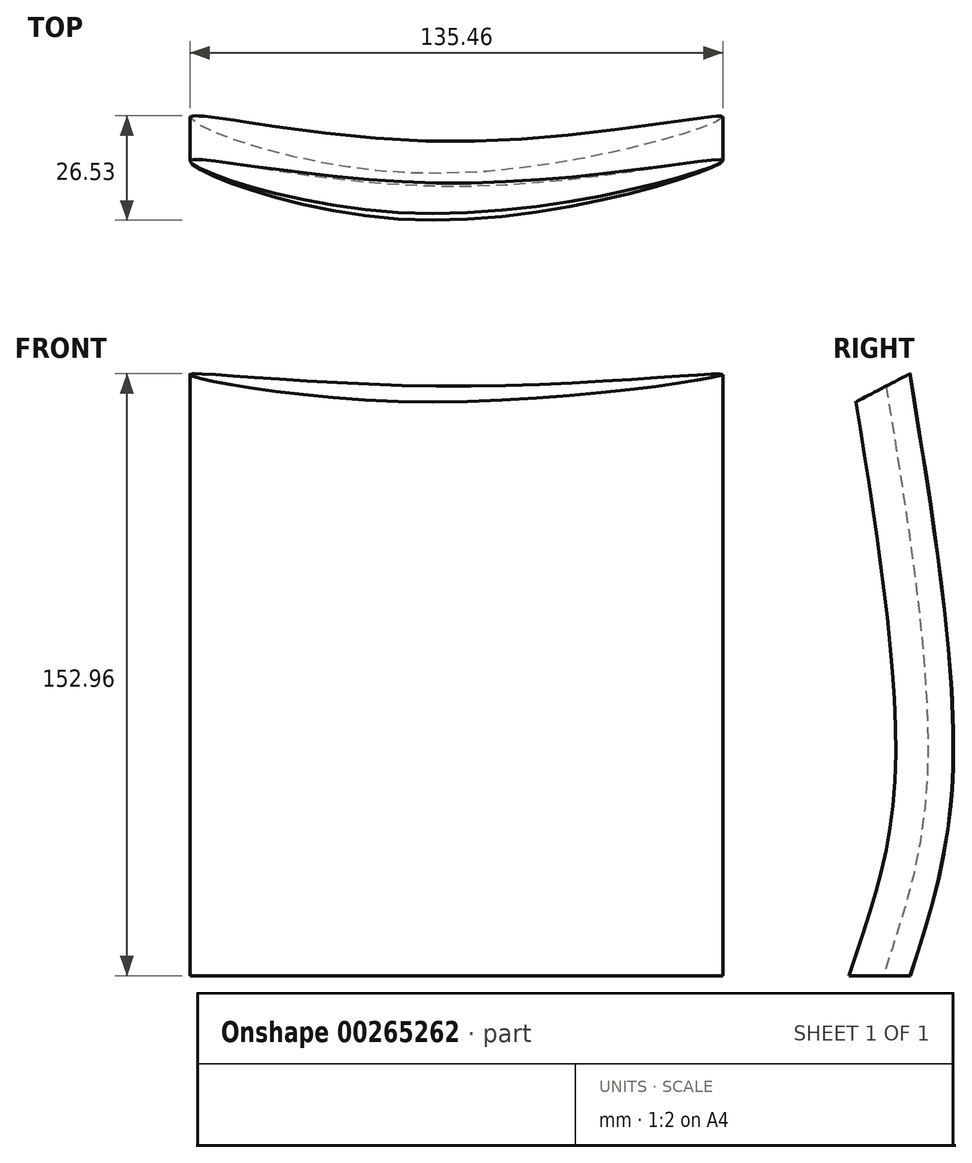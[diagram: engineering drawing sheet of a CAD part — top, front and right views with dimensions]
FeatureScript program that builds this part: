
annotation { "Feature Type Name" : "Feature", "Feature Type Description" : "" }
export const myFeature = defineFeature(function(context is Context, id is Id, definition is map)
    precondition{}
    {
        {
            var Q0;
            Q0=qCreatedBy(makeId("Right.planeOp"),FACE);
            var sketch = newSketch(context, id + "F2", { "sketchPlane" : qUnion([Q0])});
            skFitSpline(sketch, "E0", {"points": [v(0, 0) * mm, v(10.77, 48.56) * mm, v(0, 152.79) * mm], "startDerivative": vector(35.5, 107.42) * mm, "endDerivative": vector(-31.4, 192.9) * mm});
            skSolve(sketch);
        }
        {
            var Q0;
            Q0=qCreatedBy(makeId("Top.planeOp"),FACE);
            var sketch = newSketch(context, id + "F3", { "sketchPlane" : qUnion([Q0])});
            skFitSpline(sketch, "E1", {"points": [v(-59.08, 0) * mm, v(6.48, -6.45) * mm, v(76.36, 0) * mm, v(0, -15.1) * mm, v(-59.08, 0) * mm]});
            skSolve(sketch);
        }
        {
            var Q0;
            Q0=makeQuery(id+"F3.imprint","IMPRINT",FACE,{"disambiguationData":[TD([[makeQuery(id+"F3.imprint","IMPRINT",EDGE,{"derivedFrom":sQuery(id+"F3.wireOp",EDGE,"E1")}),-1.0]])]});
            var Q1;
            Q1=sQuery(id+"F2.wireOp",EDGE,"E0");
            sweep(context, id + "F0", {"profiles" : qUnion([Q0]), "path" : qUnion([Q1])});
        }
    });
